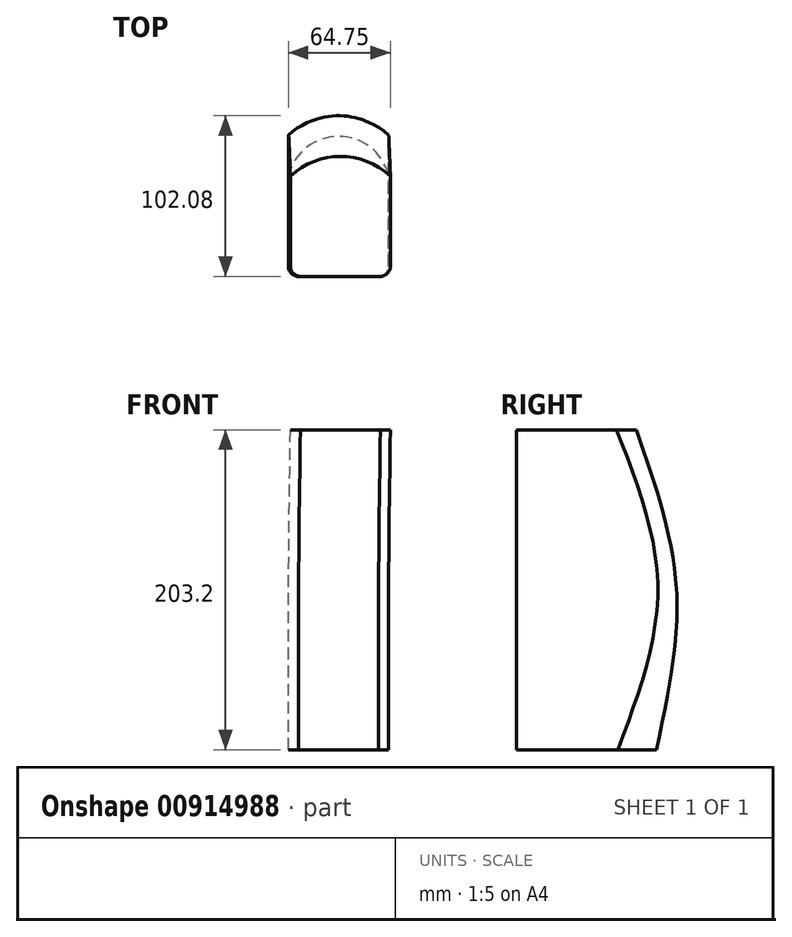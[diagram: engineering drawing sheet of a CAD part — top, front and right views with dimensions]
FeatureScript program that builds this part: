
annotation { "Feature Type Name" : "Feature", "Feature Type Description" : "" }
export const myFeature = defineFeature(function(context is Context, id is Id, definition is map)
    precondition{}
    {
        {
            var Q0;
            Q0=qCreatedBy(makeId("Front.planeOp"),FACE);
            var sketch = newSketch(context, id + "F0", { "sketchPlane" : qUnion([Q0])});
            skLineSegment(sketch, "E0", {"start": v(0, 0) * mm, "end": v(0, 104.1) * mm});
            skLineSegment(sketch, "E1", {"start": v(0, 104.1) * mm, "end": v(0, 203.2) * mm});
            skSolve(sketch);
        }
        {
            var Q0;
            Q0=qCreatedBy(makeId("Top.planeOp"),FACE);
            var sketch = newSketch(context, id + "F1", { "sketchPlane" : qUnion([Q0])});
            skLineSegment(sketch, "E2.bottom", {"start": v(-25.4, 0) * mm, "end": v(25.4, 0) * mm});
            skLineSegment(sketch, "E2.top", {"start": v(-31.75, 64.54) * mm, "end": v(31.75, 64.54) * mm, "construction": true});
            skLineSegment(sketch, "E2.left", {"start": v(-31.75, 6.35) * mm, "end": v(-31.75, 64.54) * mm});
            skLineSegment(sketch, "E2.right", {"start": v(31.75, 6.35) * mm, "end": v(31.75, 64.54) * mm});
            skArc(sketch, "E3", {"start": v(31.75, 64.54) * mm, "mid": v(0, 88.9) * mm, "end": v(-31.75, 64.54) * mm});
            skPoint(sketch, "E4.visualSharp", {"position": v(-31.75, 0) * mm});
            skArc(sketch, "E4.filletArc", {"start": v(-31.75, 6.35) * mm, "mid": v(-29.9, 1.86) * mm, "end": v(-25.4, 0) * mm});
            skPoint(sketch, "E5.visualSharp", {"position": v(31.75, 0) * mm});
            skArc(sketch, "E5.filletArc", {"start": v(25.4, 0) * mm, "mid": v(29.9, 1.86) * mm, "end": v(31.75, 6.35) * mm});
            skSolve(sketch);
        }
        {
            var Q0;
            Q0=qCreatedBy(makeId("Top.planeOp"),FACE);
            var Q1;
            Q1=sQuery(id+"F0.wireOp",VERTEX,"E1.end");
            cPlane(context, id + "F2", {"entities" : qUnion([Q0, Q1]), "cplaneType" : CPlaneType.PLANE_POINT, "offset" : 25.4 * mm, "width" : 152.4 * mm, "height" : 152.4 * mm});
        }
        {
            var Q0;
            Q0=qCreatedBy(id+"F2.planeOp",FACE);
            var sketch = newSketch(context, id + "F3", { "sketchPlane" : qUnion([Q0])});
            skLineSegment(sketch, "E6.bottom", {"start": v(-24.27, 0) * mm, "end": v(26.53, 0) * mm});
            skLineSegment(sketch, "E6.top", {"start": v(-30.62, 63.65) * mm, "end": v(32.88, 63.65) * mm, "construction": true});
            skLineSegment(sketch, "E6.left", {"start": v(-30.62, 6.35) * mm, "end": v(-30.62, 63.65) * mm});
            skLineSegment(sketch, "E6.right", {"start": v(32.88, 6.35) * mm, "end": v(32.88, 63.65) * mm});
            skArc(sketch, "E7", {"start": v(32.88, 63.65) * mm, "mid": v(1.13, 76.2) * mm, "end": v(-30.62, 63.65) * mm});
            skPoint(sketch, "E8.visualSharp", {"position": v(-30.62, 0) * mm});
            skArc(sketch, "E8.filletArc", {"start": v(-30.62, 6.35) * mm, "mid": v(-28.76, 1.86) * mm, "end": v(-24.27, 0) * mm});
            skPoint(sketch, "E9.visualSharp", {"position": v(32.88, 0) * mm});
            skArc(sketch, "E9.filletArc", {"start": v(26.53, 0) * mm, "mid": v(31.02, 1.86) * mm, "end": v(32.88, 6.35) * mm});
            skSolve(sketch);
        }
        {
            var Q0;
            Q0=qCreatedBy(makeId("Top.planeOp"),FACE);
            var Q1;
            Q1=sQuery(id+"F0.wireOp",VERTEX,"E0.end");
            cPlane(context, id + "F4", {"entities" : qUnion([Q0, Q1]), "cplaneType" : CPlaneType.PLANE_POINT, "offset" : 25.4 * mm, "width" : 152.4 * mm, "height" : 152.4 * mm});
        }
        {
            var Q0;
            Q0=qCreatedBy(id+"F4.planeOp",FACE);
            var sketch = newSketch(context, id + "F5", { "sketchPlane" : qUnion([Q0])});
            skLineSegment(sketch, "E10.bottom", {"start": v(-25.4, 0) * mm, "end": v(25.4, 0) * mm});
            skLineSegment(sketch, "E10.top", {"start": v(-31.75, 89.86) * mm, "end": v(31.75, 89.86) * mm, "construction": true});
            skLineSegment(sketch, "E10.left", {"start": v(-31.75, 6.35) * mm, "end": v(-31.75, 89.86) * mm});
            skLineSegment(sketch, "E10.right", {"start": v(31.75, 6.35) * mm, "end": v(31.75, 89.86) * mm});
            skArc(sketch, "E11", {"start": v(31.75, 89.86) * mm, "mid": v(0, 101.6) * mm, "end": v(-31.75, 89.86) * mm});
            skPoint(sketch, "E12.visualSharp", {"position": v(-31.75, 0) * mm});
            skArc(sketch, "E12.filletArc", {"start": v(-31.75, 6.35) * mm, "mid": v(-29.9, 1.86) * mm, "end": v(-25.4, 0) * mm});
            skPoint(sketch, "E13.visualSharp", {"position": v(31.75, 0) * mm});
            skArc(sketch, "E13.filletArc", {"start": v(25.4, 0) * mm, "mid": v(29.9, 1.86) * mm, "end": v(31.75, 6.35) * mm});
            skSolve(sketch);
        }
        {
            var Q0;
            Q0=makeQuery(id+"F1.imprint","IMPRINT",FACE,{"disambiguationData":[TD([[makeQuery(id+"F1.imprint","IMPRINT",EDGE,{"derivedFrom":sQuery(id+"F1.wireOp",EDGE,"E2.bottom")}),1.0]])]});
            var Q1;
            Q1=makeQuery(id+"F5.imprint","IMPRINT",FACE,{"disambiguationData":[TD([[makeQuery(id+"F5.imprint","IMPRINT",EDGE,{"derivedFrom":sQuery(id+"F5.wireOp",EDGE,"E10.bottom")}),1.0]])]});
            var Q2;
            Q2=makeQuery(id+"F3.imprint","IMPRINT",FACE,{"disambiguationData":[TD([[makeQuery(id+"F3.imprint","IMPRINT",EDGE,{"derivedFrom":sQuery(id+"F3.wireOp",EDGE,"E6.bottom")}),1.0]])]});
            loft(context, id + "F6", {"sheetProfilesArray" : [{ "sheetProfileEntities" : qUnion([Q0]) }, { "sheetProfileEntities" : qUnion([Q1]) }, { "sheetProfileEntities" : qUnion([Q2]) }]});
        }
    });
